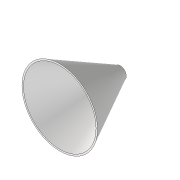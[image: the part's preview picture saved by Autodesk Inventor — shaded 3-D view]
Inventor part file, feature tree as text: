
AUTODESK INVENTOR PART (.ipt)
format: ipt  version: 2020 (Build 240168000, 168)  size: 95,744 bytes
history: native  units: mm
features: revolve x1, sketch x1
ambient origin geometry x8: Origin, YZ Plane, XZ Plane, XY Plane, X Axis, Y Axis, Z Axis, Center Point
bodies: Volumenkörper1 (feature_tree)
feature tree (2):
  revolve  "Umdrehung1"
  sketch  "Skizze2"  dims[d2=15.0mm d3=20.0mm d4=100.0mm d5=120.0mm d6=90.0deg]
